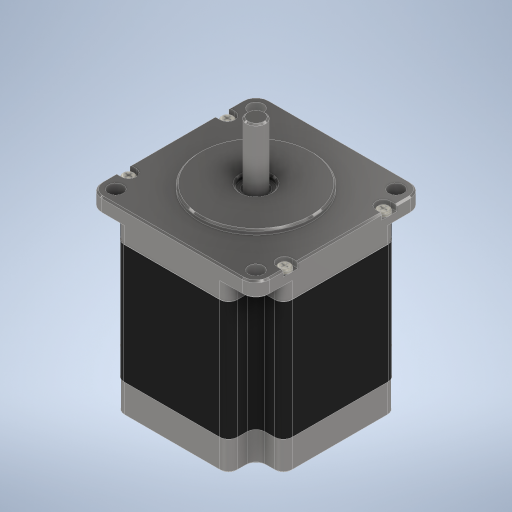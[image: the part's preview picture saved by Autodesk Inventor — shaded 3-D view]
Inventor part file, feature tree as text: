
AUTODESK INVENTOR PART (.ipt)
format: ipt  version: 2023 (Build 270158000, 158)  size: 1,088,000 bytes
history: native  units: mm
features: sketch x15, extrude x12, fillet x4, chamfer x4, projected_geometry x2, plane x1, sweep x1
ambient origin geometry x8: Origin, YZ Plane, XZ Plane, XY Plane, X Axis, Y Axis, Z Axis, Center Point
bodies: Solid1 (feature_tree)
feature tree (39):
  extrude  "Extrusion1"  Depth=38.0mm
  extrude  "Extrusion2"  Depth=28.2mm
  extrude  "Extrusion3"  Depth=10.0mm TaperAngle=0.0deg
  extrude  "Extrusion4"  Depth=40.0mm TaperAngle=0.0deg
  extrude  "Extrusion5"  Depth=56.4mm
  extrude  "Extrusion6"  Depth=5.0mm TaperAngle=0.0deg
  extrude  "Extrusion7"  Depth=1.6mm TaperAngle=0.0deg
  extrude  "Extrusion8"  Depth=1.6mm TaperAngle=0.0deg
  fillet  "Fillet1"  Radius=6.65mm
  extrude  "Extrusion9"  Depth=26.0mm
  fillet  "Fillet2"  Radius=26.0mm
  chamfer  "Chamfer1"  Distance=26.0mm
  chamfer  "Chamfer2"  Distance=2.0mm Angle=45.0deg
  chamfer  "Chamfer4"  Distance=2.0mm Angle=45.0deg
  extrude  "Extrusion10"  Depth=5.0mm
  extrude  "Extrusion11"  Depth=2.5mm
  fillet  "Fillet3"  Radius=2.0mm
  extrude  "Extrusion12"  Depth=2.0mm
  fillet  "Fillet4"  Radius=1.25mm
  sketch  "Sketch13"  dims[d44=4.65mm d45=0.5mm d46=2.0mm d47=45.0deg d48=0.5mm d49=2.0mm d50=45.0deg]
  plane  "Work Plane1"
  sweep  "Sweep1"
  chamfer  "Chamfer5"  Distance=2.5mm
  sketch  "Sketch1"  dims[d7=56.4mm d8=38.0mm]
  sketch  "Sketch2"  dims[d9=28.2mm d10=28.2mm]
  projected_geometry  "Projected Loop1"
  sketch  "Sketch3"  dims[d12=38.0mm d13=10.0mm d14=0.0mm]
  projected_geometry  "Projected Loop2"
  sketch  "Sketch4"  dims[d15=0.1mm d16=40.0mm d17=0.0mm]
  sketch  "Sketch5"  dims[d18=5.0mm d19=0.0mm d20=56.4mm]
  sketch  "Sketch6"  dims[d21=56.4mm d22=5.0mm d23=0.0mm]
  sketch  "Sketch7"  dims[d24=38.0mm d25=1.6mm d26=0.0mm]
  sketch  "Sketch8"  dims[d27=10.0mm d28=1.6mm d29=0.0mm d30=6.65mm]
  sketch  "Sketch9"  dims[d31=5.0mm d32=0.0mm d33=6.35mm d34=26.0mm d35=0.0mm]
  sketch  "Sketch10"  dims[d36=3.0mm]
  sketch  "Sketch11"  dims[d40=47.1mm]
  sketch  "Sketch12"  dims[d41=5.0mm d42=26.0mm d43=0.0mm]
  sketch  "Sketch14"  dims[d54=0.5mm d55=2.0mm d56=45.0deg d57=5.0mm d58=2.5mm d60=2.0mm d61=0.0mm d62=4.0mm d63=1.25mm d64=0.0mm d65=0.6mm d66=2.5mm d67=2.5mm d68=0.4mm d69=1.25mm d70=1.25mm d71=1.0mm d72=0.0mm d73=0.3mm d75=0.0mm d76=0.15mm d77=0.519615mm d78=770.0mm d80=0.519615mm d81=10.0mm d83=10.0mm d85=0.519615mm d86=770.0mm d88=0.519615mm d89=10.0mm d91=10.0mm d93=0.0mm d94=0.0mm d95=0.5mm d96=2.0mm d97=45.0deg]
  sketch  "3D Sketch1"
